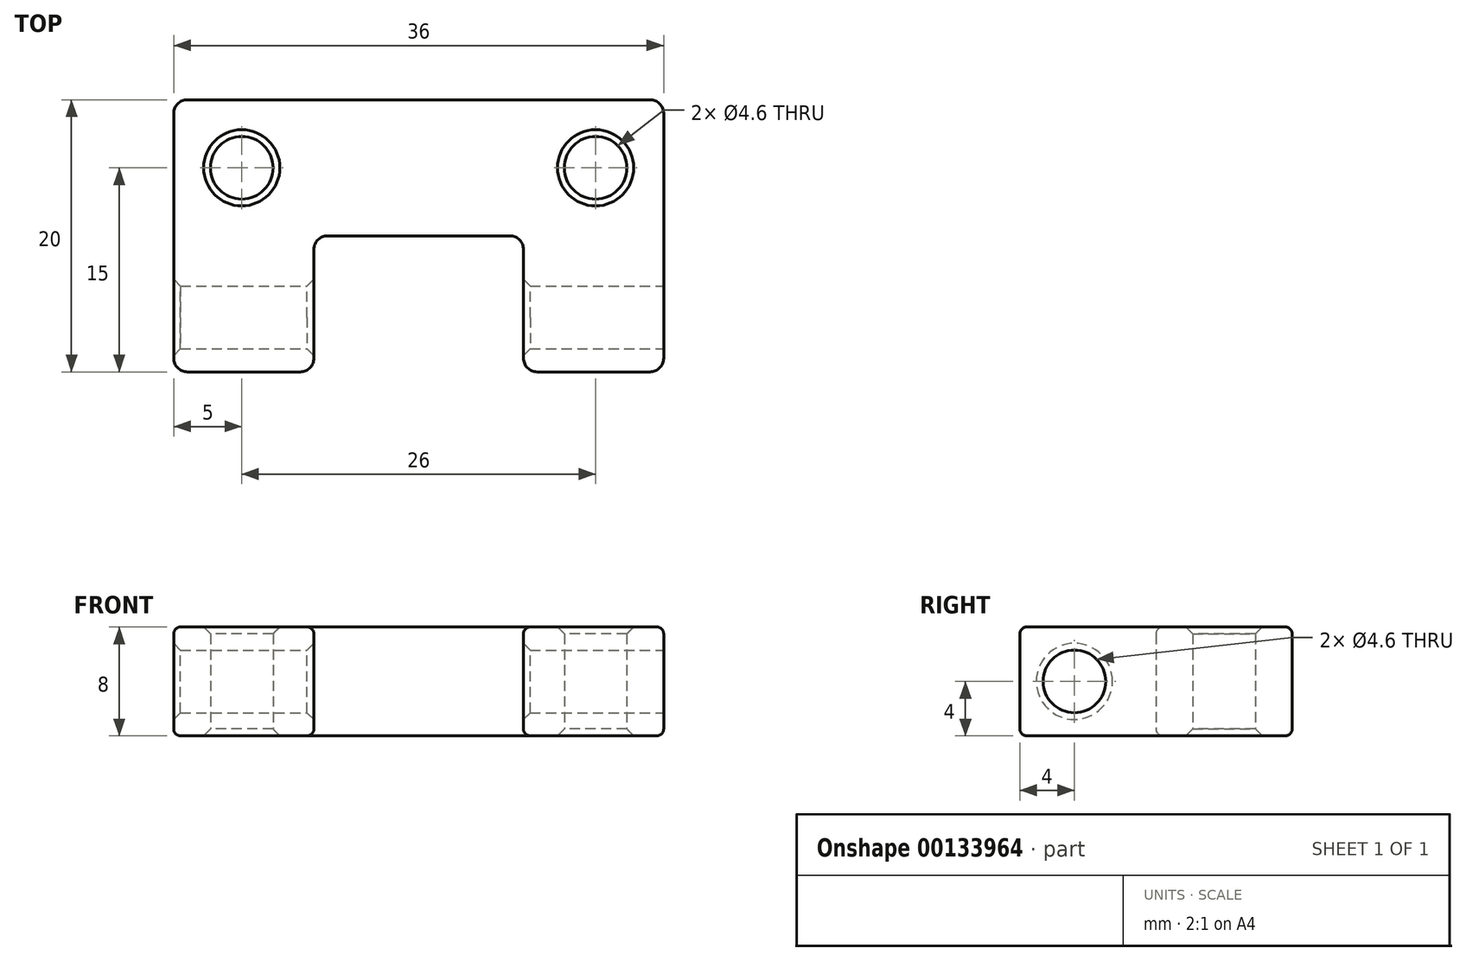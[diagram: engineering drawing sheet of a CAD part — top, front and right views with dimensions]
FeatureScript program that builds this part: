
annotation { "Feature Type Name" : "Feature", "Feature Type Description" : "" }
export const myFeature = defineFeature(function(context is Context, id is Id, definition is map)
    precondition{}
    {
        {
            var Q0;
            Q0=qCreatedBy(makeId("Top.planeOp"),FACE);
            var sketch = newSketch(context, id + "F0", { "sketchPlane" : qUnion([Q0])});
            skLineSegment(sketch, "E0", {"start": v(0, 0) * mm, "end": v(18, 0) * mm});
            skLineSegment(sketch, "E1", {"start": v(18, 0) * mm, "end": v(18, -20) * mm});
            skLineSegment(sketch, "E2", {"start": v(18, -20) * mm, "end": v(7.7, -20) * mm});
            skLineSegment(sketch, "E3", {"start": v(7.7, -20) * mm, "end": v(7.7, -11) * mm});
            skLineSegment(sketch, "E4", {"start": v(6.7, -10) * mm, "end": v(0, -10) * mm});
            skCircle(sketch, "E5", {"center": v(13, -5) * mm, "radius": 2.3 * mm});
            skLineSegment(sketch, "E6", {"start": v(0, 22.45) * mm, "end": v(0, -48.8) * mm, "construction": true});
            skLineSegment(sketch, "E7.MirrorCS", {"start": v(-18, -20) * mm, "end": v(-7.7, -20) * mm});
            skLineSegment(sketch, "E8.MirrorCS", {"start": v(-18, 0) * mm, "end": v(-18, -20) * mm});
            skLineSegment(sketch, "E9.MirrorCS", {"start": v(0, 0) * mm, "end": v(-18, 0) * mm});
            skCircle(sketch, "E10.MirrorC", {"center": v(-13, -5) * mm, "radius": 2.3 * mm});
            skPoint(sketch, "E11.visualSharp", {"position": v(7.7, -10) * mm});
            skArc(sketch, "E11.filletArc", {"start": v(7.7, -11) * mm, "mid": v(7.4, -10.3) * mm, "end": v(6.7, -10) * mm});
            skArc(sketch, "E12.MirrorCS", {"start": v(-7.7, -11) * mm, "mid": v(-7.4, -10.3) * mm, "end": v(-6.7, -10) * mm});
            skLineSegment(sketch, "E13.MirrorCS", {"start": v(-6.7, -10) * mm, "end": v(0, -10) * mm});
            skLineSegment(sketch, "E14.MirrorCS", {"start": v(-7.7, -20) * mm, "end": v(-7.7, -11) * mm});
            skSolve(sketch);
        }
        {
            var Q0;
            Q0 = qSketchRegion(id + "F0", true);
            extrude(context, id + "F1", {"entities" : qUnion([Q0]), "depth" : 8 * mm, "offsetDistance" : 25 * mm});
        }
        {
            var Q0;
            Q0=makeQuery(id+"F1.opExtrude","SWEPT_FACE",FACE,{"disambiguationData":[OSD([sQuery(id+"F0.wireOp",EDGE,"E1")])]});
            var sketch = newSketch(context, id + "F2", { "sketchPlane" : qUnion([Q0])});
            skCircle(sketch, "E15", {"center": v(-16, 4) * mm, "radius": 2.3 * mm});
            skSolve(sketch);
        }
        {
            var Q0;
            Q0 = qSketchRegion(id + "F2", true);
            extrude(context, id + "F3", {"entities" : qUnion([Q0]), "operationType" : NewBodyOperationType.REMOVE, "endBound" : BoundingType.THROUGH_ALL, "oppositeDirection" : true, "depth" : 25 * mm, "offsetDistance" : 25 * mm});
        }
        {
            var Q0;
            Q0=makeQuery(id+"F1.opExtrude","SWEPT_EDGE",EDGE,{"disambiguationData":[OSD([sQuery(id+"F0.wireOp",EDGE,"E7.MirrorCS"),sQuery(id+"F0.wireOp",EDGE,"E8.MirrorCS")])]});
            var Q1;
            Q1=makeQuery(id+"F1.opExtrude","SWEPT_EDGE",EDGE,{"disambiguationData":[OSD([sQuery(id+"F0.wireOp",EDGE,"E2"),sQuery(id+"F0.wireOp",EDGE,"E3")])]});
            var Q2;
            Q2=makeQuery(id+"F1.opExtrude","SWEPT_EDGE",EDGE,{"disambiguationData":[OSD([sQuery(id+"F0.wireOp",EDGE,"E1"),sQuery(id+"F0.wireOp",EDGE,"E2")])]});
            var Q3;
            Q3=makeQuery(id+"F1.opExtrude","SWEPT_EDGE",EDGE,{"disambiguationData":[OSD([sQuery(id+"F0.wireOp",EDGE,"E8.MirrorCS"),sQuery(id+"F0.wireOp",EDGE,"E9.MirrorCS")])]});
            var Q4;
            Q4=makeQuery(id+"F1.opExtrude","SWEPT_EDGE",EDGE,{"disambiguationData":[OSD([sQuery(id+"F0.wireOp",EDGE,"E0"),sQuery(id+"F0.wireOp",EDGE,"E1")])]});
            var Q5;
            Q5=makeQuery(id+"F1.opExtrude","SWEPT_EDGE",EDGE,{"disambiguationData":[OSD([sQuery(id+"F0.wireOp",EDGE,"E7.MirrorCS"),sQuery(id+"F0.wireOp",EDGE,"E14.MirrorCS")])]});
            fillet(context, id + "F4", {"entities" : qUnion([Q0, Q1, Q2, Q3, Q4, Q5]), "radius" : 1 * mm, "tangentPropagation" : true, "allowEdgeOverflow" : false});
        }
        {
            var Q0;
            Q0=makeQuery(id+"F1.opExtrude","CAP_EDGE",EDGE,{"disambiguationData":[OSD([sQuery(id+"F0.wireOp",EDGE,"E10.MirrorC")])],"isStart":false});
            var Q1;
            Q1=makeQuery(id+"F1.opExtrude","CAP_EDGE",EDGE,{"disambiguationData":[OSD([sQuery(id+"F0.wireOp",EDGE,"E5")])],"isStart":false});
            var Q2;
            Q2=makeQuery(id+"F1.opExtrude","CAP_EDGE",EDGE,{"disambiguationData":[OSD([sQuery(id+"F0.wireOp",EDGE,"E10.MirrorC")])],"isStart":true});
            var Q3;
            Q3=makeQuery(id+"F1.opExtrude","CAP_EDGE",EDGE,{"disambiguationData":[OSD([sQuery(id+"F0.wireOp",EDGE,"E5")])],"isStart":true});
            var Q4;
            Q4=makeQuery(id+"F3.boolean.opBoolean","INTERSECT",EDGE,{"derivedFrom":[makeQuery(id+"F1.opExtrude","SWEPT_FACE",FACE,{"disambiguationData":[OSD([sQuery(id+"F0.wireOp",EDGE,"E14.MirrorCS")])]}),makeQuery(id+"F3.opExtrude","SWEPT_FACE",FACE,{"disambiguationData":[OSD([sQuery(id+"F2.wireOp",EDGE,"E15")])]})]});
            var Q5;
            Q5=makeQuery(id+"F3.boolean.opBoolean","INTERSECT",EDGE,{"derivedFrom":[makeQuery(id+"F1.opExtrude","SWEPT_FACE",FACE,{"disambiguationData":[OSD([sQuery(id+"F0.wireOp",EDGE,"E8.MirrorCS")])]}),makeQuery(id+"F3.opExtrude","SWEPT_FACE",FACE,{"disambiguationData":[OSD([sQuery(id+"F2.wireOp",EDGE,"E15")])]})]});
            var Q6;
            Q6=makeQuery(id+"F3.boolean.opBoolean","INTERSECT",EDGE,{"derivedFrom":[makeQuery(id+"F1.opExtrude","SWEPT_FACE",FACE,{"disambiguationData":[OSD([sQuery(id+"F0.wireOp",EDGE,"E3")])]}),makeQuery(id+"F3.opExtrude","SWEPT_FACE",FACE,{"disambiguationData":[OSD([sQuery(id+"F2.wireOp",EDGE,"E15")])]})]});
            var Q7;
            Q7=makeQuery(id+"F3.boolean.opBoolean","COPY",EDGE,{"derivedFrom":makeQuery(id+"F3.opExtrude","CAP_EDGE",EDGE,{"disambiguationData":[OSD([sQuery(id+"F2.wireOp",EDGE,"E15")])],"isStart":true})});
            chamfer(context, id + "F5", {"entities" : qUnion([Q0, Q1, Q2, Q3, Q4, Q5, Q6, Q7]), "width" : 0.5 * mm, "tangentPropagation" : true});
        }
        {
            var Q0;
            Q0=makeQuery(id+"F1.opExtrude","CAP_EDGE",EDGE,{"disambiguationData":[OSD([sQuery(id+"F0.wireOp",EDGE,"E7.MirrorCS")])],"isStart":false});
            var Q1;
            {var subQ0=sQuery(id+"F0.wireOp",EDGE,"E14.MirrorCS");var subQ1=sQuery(id+"F0.wireOp",EDGE,"E7.MirrorCS");Q1=makeQuery(id+"F4.opFillet","BLEND_EDGE",EDGE,{"blendedFrom":[makeQuery(id+"F1.opExtrude","SWEPT_EDGE",EDGE,{"disambiguationData":[OSD([subQ1,subQ0])]}),makeQuery(id+"F1.opExtrude","CAP_FACE",FACE,{"disambiguationData":[OSD([sQuery(id+"F0.wireOp",EDGE,"E0"),sQuery(id+"F0.wireOp",EDGE,"E1"),sQuery(id+"F0.wireOp",EDGE,"E2"),sQuery(id+"F0.wireOp",EDGE,"E3"),sQuery(id+"F0.wireOp",EDGE,"E4"),sQuery(id+"F0.wireOp",EDGE,"E5"),subQ1,sQuery(id+"F0.wireOp",EDGE,"E8.MirrorCS"),sQuery(id+"F0.wireOp",EDGE,"E9.MirrorCS"),sQuery(id+"F0.wireOp",EDGE,"E10.MirrorC"),sQuery(id+"F0.wireOp",EDGE,"E11.filletArc"),sQuery(id+"F0.wireOp",EDGE,"E12.MirrorCS"),sQuery(id+"F0.wireOp",EDGE,"E13.MirrorCS"),subQ0])],"isStart":false})],"blendedInto":[makeQuery(id+"F1.opExtrude","CAP_FACE",FACE,{"disambiguationData":[OSD([sQuery(id+"F0.wireOp",EDGE,"E0"),sQuery(id+"F0.wireOp",EDGE,"E1"),sQuery(id+"F0.wireOp",EDGE,"E2"),sQuery(id+"F0.wireOp",EDGE,"E3"),sQuery(id+"F0.wireOp",EDGE,"E4"),sQuery(id+"F0.wireOp",EDGE,"E5"),subQ1,sQuery(id+"F0.wireOp",EDGE,"E8.MirrorCS"),sQuery(id+"F0.wireOp",EDGE,"E9.MirrorCS"),sQuery(id+"F0.wireOp",EDGE,"E10.MirrorC"),sQuery(id+"F0.wireOp",EDGE,"E11.filletArc"),sQuery(id+"F0.wireOp",EDGE,"E12.MirrorCS"),sQuery(id+"F0.wireOp",EDGE,"E13.MirrorCS"),subQ0])],"isStart":false})]});}
            var Q2;
            Q2=makeQuery(id+"F1.opExtrude","CAP_EDGE",EDGE,{"disambiguationData":[OSD([sQuery(id+"F0.wireOp",EDGE,"E14.MirrorCS")])],"isStart":false});
            var Q3;
            Q3=makeQuery(id+"F1.opExtrude","CAP_EDGE",EDGE,{"disambiguationData":[OSD([sQuery(id+"F0.wireOp",EDGE,"E12.MirrorCS")])],"isStart":false});
            var Q4;
            Q4=makeQuery(id+"F1.opExtrude","CAP_EDGE",EDGE,{"disambiguationData":[OSD([sQuery(id+"F0.wireOp",EDGE,"E4"),sQuery(id+"F0.wireOp",EDGE,"E13.MirrorCS")])],"isStart":false});
            var Q5;
            Q5=makeQuery(id+"F1.opExtrude","CAP_EDGE",EDGE,{"disambiguationData":[OSD([sQuery(id+"F0.wireOp",EDGE,"E11.filletArc")])],"isStart":false});
            var Q6;
            Q6=makeQuery(id+"F1.opExtrude","CAP_EDGE",EDGE,{"disambiguationData":[OSD([sQuery(id+"F0.wireOp",EDGE,"E3")])],"isStart":false});
            var Q7;
            {var subQ0=sQuery(id+"F0.wireOp",EDGE,"E3");var subQ1=sQuery(id+"F0.wireOp",EDGE,"E2");Q7=makeQuery(id+"F4.opFillet","BLEND_EDGE",EDGE,{"blendedFrom":[makeQuery(id+"F1.opExtrude","SWEPT_EDGE",EDGE,{"disambiguationData":[OSD([subQ1,subQ0])]}),makeQuery(id+"F1.opExtrude","CAP_FACE",FACE,{"disambiguationData":[OSD([sQuery(id+"F0.wireOp",EDGE,"E0"),sQuery(id+"F0.wireOp",EDGE,"E1"),subQ1,subQ0,sQuery(id+"F0.wireOp",EDGE,"E4"),sQuery(id+"F0.wireOp",EDGE,"E5"),sQuery(id+"F0.wireOp",EDGE,"E7.MirrorCS"),sQuery(id+"F0.wireOp",EDGE,"E8.MirrorCS"),sQuery(id+"F0.wireOp",EDGE,"E9.MirrorCS"),sQuery(id+"F0.wireOp",EDGE,"E10.MirrorC"),sQuery(id+"F0.wireOp",EDGE,"E11.filletArc"),sQuery(id+"F0.wireOp",EDGE,"E12.MirrorCS"),sQuery(id+"F0.wireOp",EDGE,"E13.MirrorCS"),sQuery(id+"F0.wireOp",EDGE,"E14.MirrorCS")])],"isStart":false})],"blendedInto":[makeQuery(id+"F1.opExtrude","CAP_FACE",FACE,{"disambiguationData":[OSD([sQuery(id+"F0.wireOp",EDGE,"E0"),sQuery(id+"F0.wireOp",EDGE,"E1"),subQ1,subQ0,sQuery(id+"F0.wireOp",EDGE,"E4"),sQuery(id+"F0.wireOp",EDGE,"E5"),sQuery(id+"F0.wireOp",EDGE,"E7.MirrorCS"),sQuery(id+"F0.wireOp",EDGE,"E8.MirrorCS"),sQuery(id+"F0.wireOp",EDGE,"E9.MirrorCS"),sQuery(id+"F0.wireOp",EDGE,"E10.MirrorC"),sQuery(id+"F0.wireOp",EDGE,"E11.filletArc"),sQuery(id+"F0.wireOp",EDGE,"E12.MirrorCS"),sQuery(id+"F0.wireOp",EDGE,"E13.MirrorCS"),sQuery(id+"F0.wireOp",EDGE,"E14.MirrorCS")])],"isStart":false})]});}
            var Q8;
            Q8=makeQuery(id+"F1.opExtrude","CAP_EDGE",EDGE,{"disambiguationData":[OSD([sQuery(id+"F0.wireOp",EDGE,"E2")])],"isStart":false});
            var Q9;
            {var subQ0=sQuery(id+"F0.wireOp",EDGE,"E2");var subQ1=sQuery(id+"F0.wireOp",EDGE,"E1");Q9=makeQuery(id+"F4.opFillet","BLEND_EDGE",EDGE,{"blendedFrom":[makeQuery(id+"F1.opExtrude","SWEPT_EDGE",EDGE,{"disambiguationData":[OSD([subQ1,subQ0])]}),makeQuery(id+"F1.opExtrude","CAP_FACE",FACE,{"disambiguationData":[OSD([sQuery(id+"F0.wireOp",EDGE,"E0"),subQ1,subQ0,sQuery(id+"F0.wireOp",EDGE,"E3"),sQuery(id+"F0.wireOp",EDGE,"E4"),sQuery(id+"F0.wireOp",EDGE,"E5"),sQuery(id+"F0.wireOp",EDGE,"E7.MirrorCS"),sQuery(id+"F0.wireOp",EDGE,"E8.MirrorCS"),sQuery(id+"F0.wireOp",EDGE,"E9.MirrorCS"),sQuery(id+"F0.wireOp",EDGE,"E10.MirrorC"),sQuery(id+"F0.wireOp",EDGE,"E11.filletArc"),sQuery(id+"F0.wireOp",EDGE,"E12.MirrorCS"),sQuery(id+"F0.wireOp",EDGE,"E13.MirrorCS"),sQuery(id+"F0.wireOp",EDGE,"E14.MirrorCS")])],"isStart":false})],"blendedInto":[makeQuery(id+"F1.opExtrude","CAP_FACE",FACE,{"disambiguationData":[OSD([sQuery(id+"F0.wireOp",EDGE,"E0"),subQ1,subQ0,sQuery(id+"F0.wireOp",EDGE,"E3"),sQuery(id+"F0.wireOp",EDGE,"E4"),sQuery(id+"F0.wireOp",EDGE,"E5"),sQuery(id+"F0.wireOp",EDGE,"E7.MirrorCS"),sQuery(id+"F0.wireOp",EDGE,"E8.MirrorCS"),sQuery(id+"F0.wireOp",EDGE,"E9.MirrorCS"),sQuery(id+"F0.wireOp",EDGE,"E10.MirrorC"),sQuery(id+"F0.wireOp",EDGE,"E11.filletArc"),sQuery(id+"F0.wireOp",EDGE,"E12.MirrorCS"),sQuery(id+"F0.wireOp",EDGE,"E13.MirrorCS"),sQuery(id+"F0.wireOp",EDGE,"E14.MirrorCS")])],"isStart":false})]});}
            var Q10;
            Q10=makeQuery(id+"F1.opExtrude","CAP_EDGE",EDGE,{"disambiguationData":[OSD([sQuery(id+"F0.wireOp",EDGE,"E1")])],"isStart":false});
            var Q11;
            {var subQ0=sQuery(id+"F0.wireOp",EDGE,"E1");var subQ1=sQuery(id+"F0.wireOp",EDGE,"E0");Q11=makeQuery(id+"F4.opFillet","BLEND_EDGE",EDGE,{"blendedFrom":[makeQuery(id+"F1.opExtrude","SWEPT_EDGE",EDGE,{"disambiguationData":[OSD([subQ1,subQ0])]}),makeQuery(id+"F1.opExtrude","CAP_FACE",FACE,{"disambiguationData":[OSD([subQ1,subQ0,sQuery(id+"F0.wireOp",EDGE,"E2"),sQuery(id+"F0.wireOp",EDGE,"E3"),sQuery(id+"F0.wireOp",EDGE,"E4"),sQuery(id+"F0.wireOp",EDGE,"E5"),sQuery(id+"F0.wireOp",EDGE,"E7.MirrorCS"),sQuery(id+"F0.wireOp",EDGE,"E8.MirrorCS"),sQuery(id+"F0.wireOp",EDGE,"E9.MirrorCS"),sQuery(id+"F0.wireOp",EDGE,"E10.MirrorC"),sQuery(id+"F0.wireOp",EDGE,"E11.filletArc"),sQuery(id+"F0.wireOp",EDGE,"E12.MirrorCS"),sQuery(id+"F0.wireOp",EDGE,"E13.MirrorCS"),sQuery(id+"F0.wireOp",EDGE,"E14.MirrorCS")])],"isStart":false})],"blendedInto":[makeQuery(id+"F1.opExtrude","CAP_FACE",FACE,{"disambiguationData":[OSD([subQ1,subQ0,sQuery(id+"F0.wireOp",EDGE,"E2"),sQuery(id+"F0.wireOp",EDGE,"E3"),sQuery(id+"F0.wireOp",EDGE,"E4"),sQuery(id+"F0.wireOp",EDGE,"E5"),sQuery(id+"F0.wireOp",EDGE,"E7.MirrorCS"),sQuery(id+"F0.wireOp",EDGE,"E8.MirrorCS"),sQuery(id+"F0.wireOp",EDGE,"E9.MirrorCS"),sQuery(id+"F0.wireOp",EDGE,"E10.MirrorC"),sQuery(id+"F0.wireOp",EDGE,"E11.filletArc"),sQuery(id+"F0.wireOp",EDGE,"E12.MirrorCS"),sQuery(id+"F0.wireOp",EDGE,"E13.MirrorCS"),sQuery(id+"F0.wireOp",EDGE,"E14.MirrorCS")])],"isStart":false})]});}
            var Q12;
            Q12=makeQuery(id+"F1.opExtrude","CAP_EDGE",EDGE,{"disambiguationData":[OSD([sQuery(id+"F0.wireOp",EDGE,"E0"),sQuery(id+"F0.wireOp",EDGE,"E9.MirrorCS")])],"isStart":false});
            var Q13;
            {var subQ0=sQuery(id+"F0.wireOp",EDGE,"E9.MirrorCS");var subQ1=sQuery(id+"F0.wireOp",EDGE,"E8.MirrorCS");Q13=makeQuery(id+"F4.opFillet","BLEND_EDGE",EDGE,{"blendedFrom":[makeQuery(id+"F1.opExtrude","SWEPT_EDGE",EDGE,{"disambiguationData":[OSD([subQ1,subQ0])]}),makeQuery(id+"F1.opExtrude","CAP_FACE",FACE,{"disambiguationData":[OSD([sQuery(id+"F0.wireOp",EDGE,"E0"),sQuery(id+"F0.wireOp",EDGE,"E1"),sQuery(id+"F0.wireOp",EDGE,"E2"),sQuery(id+"F0.wireOp",EDGE,"E3"),sQuery(id+"F0.wireOp",EDGE,"E4"),sQuery(id+"F0.wireOp",EDGE,"E5"),sQuery(id+"F0.wireOp",EDGE,"E7.MirrorCS"),subQ1,subQ0,sQuery(id+"F0.wireOp",EDGE,"E10.MirrorC"),sQuery(id+"F0.wireOp",EDGE,"E11.filletArc"),sQuery(id+"F0.wireOp",EDGE,"E12.MirrorCS"),sQuery(id+"F0.wireOp",EDGE,"E13.MirrorCS"),sQuery(id+"F0.wireOp",EDGE,"E14.MirrorCS")])],"isStart":false})],"blendedInto":[makeQuery(id+"F1.opExtrude","CAP_FACE",FACE,{"disambiguationData":[OSD([sQuery(id+"F0.wireOp",EDGE,"E0"),sQuery(id+"F0.wireOp",EDGE,"E1"),sQuery(id+"F0.wireOp",EDGE,"E2"),sQuery(id+"F0.wireOp",EDGE,"E3"),sQuery(id+"F0.wireOp",EDGE,"E4"),sQuery(id+"F0.wireOp",EDGE,"E5"),sQuery(id+"F0.wireOp",EDGE,"E7.MirrorCS"),subQ1,subQ0,sQuery(id+"F0.wireOp",EDGE,"E10.MirrorC"),sQuery(id+"F0.wireOp",EDGE,"E11.filletArc"),sQuery(id+"F0.wireOp",EDGE,"E12.MirrorCS"),sQuery(id+"F0.wireOp",EDGE,"E13.MirrorCS"),sQuery(id+"F0.wireOp",EDGE,"E14.MirrorCS")])],"isStart":false})]});}
            var Q14;
            Q14=makeQuery(id+"F1.opExtrude","CAP_EDGE",EDGE,{"disambiguationData":[OSD([sQuery(id+"F0.wireOp",EDGE,"E8.MirrorCS")])],"isStart":false});
            var Q15;
            {var subQ0=sQuery(id+"F0.wireOp",EDGE,"E8.MirrorCS");var subQ1=sQuery(id+"F0.wireOp",EDGE,"E7.MirrorCS");Q15=makeQuery(id+"F4.opFillet","BLEND_EDGE",EDGE,{"blendedFrom":[makeQuery(id+"F1.opExtrude","SWEPT_EDGE",EDGE,{"disambiguationData":[OSD([subQ1,subQ0])]}),makeQuery(id+"F1.opExtrude","CAP_FACE",FACE,{"disambiguationData":[OSD([sQuery(id+"F0.wireOp",EDGE,"E0"),sQuery(id+"F0.wireOp",EDGE,"E1"),sQuery(id+"F0.wireOp",EDGE,"E2"),sQuery(id+"F0.wireOp",EDGE,"E3"),sQuery(id+"F0.wireOp",EDGE,"E4"),sQuery(id+"F0.wireOp",EDGE,"E5"),subQ1,subQ0,sQuery(id+"F0.wireOp",EDGE,"E9.MirrorCS"),sQuery(id+"F0.wireOp",EDGE,"E10.MirrorC"),sQuery(id+"F0.wireOp",EDGE,"E11.filletArc"),sQuery(id+"F0.wireOp",EDGE,"E12.MirrorCS"),sQuery(id+"F0.wireOp",EDGE,"E13.MirrorCS"),sQuery(id+"F0.wireOp",EDGE,"E14.MirrorCS")])],"isStart":false})],"blendedInto":[makeQuery(id+"F1.opExtrude","CAP_FACE",FACE,{"disambiguationData":[OSD([sQuery(id+"F0.wireOp",EDGE,"E0"),sQuery(id+"F0.wireOp",EDGE,"E1"),sQuery(id+"F0.wireOp",EDGE,"E2"),sQuery(id+"F0.wireOp",EDGE,"E3"),sQuery(id+"F0.wireOp",EDGE,"E4"),sQuery(id+"F0.wireOp",EDGE,"E5"),subQ1,subQ0,sQuery(id+"F0.wireOp",EDGE,"E9.MirrorCS"),sQuery(id+"F0.wireOp",EDGE,"E10.MirrorC"),sQuery(id+"F0.wireOp",EDGE,"E11.filletArc"),sQuery(id+"F0.wireOp",EDGE,"E12.MirrorCS"),sQuery(id+"F0.wireOp",EDGE,"E13.MirrorCS"),sQuery(id+"F0.wireOp",EDGE,"E14.MirrorCS")])],"isStart":false})]});}
            var Q16;
            Q16=makeQuery(id+"F1.opExtrude","CAP_EDGE",EDGE,{"disambiguationData":[OSD([sQuery(id+"F0.wireOp",EDGE,"E14.MirrorCS")])],"isStart":true});
            fillet(context, id + "F6", {"entities" : qUnion([Q0, Q1, Q2, Q3, Q4, Q5, Q6, Q7, Q8, Q9, Q10, Q11, Q12, Q13, Q14, Q15, Q16]), "radius" : 0.5 * mm, "tangentPropagation" : true, "allowEdgeOverflow" : false});
        }
    });
